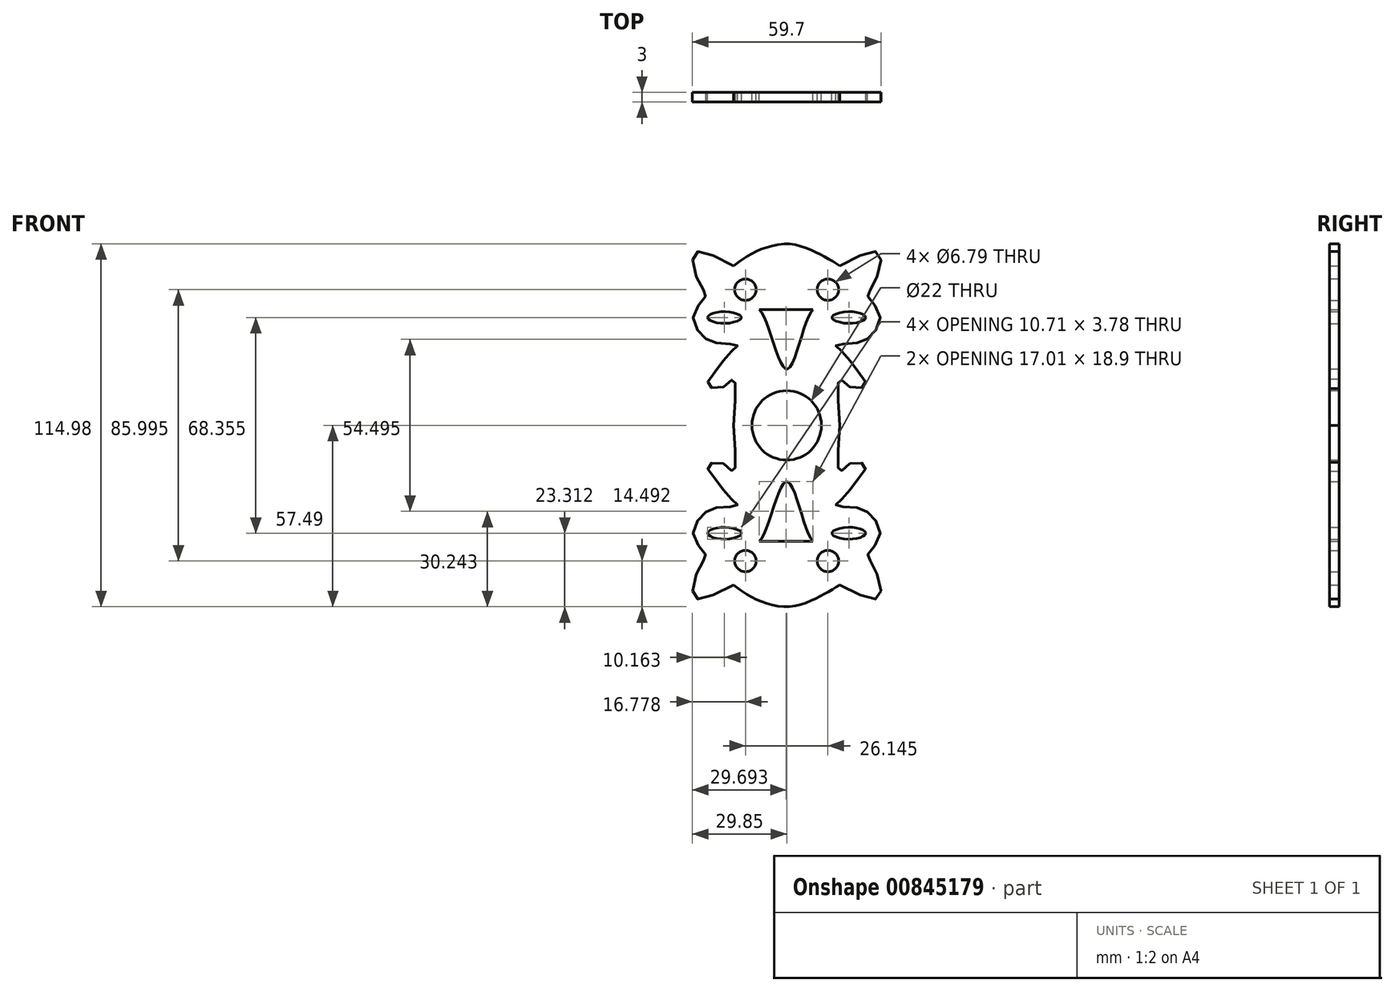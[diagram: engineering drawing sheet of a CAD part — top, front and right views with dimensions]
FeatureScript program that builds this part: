
annotation { "Feature Type Name" : "Feature", "Feature Type Description" : "" }
export const myFeature = defineFeature(function(context is Context, id is Id, definition is map)
    precondition{}
    {
        {
            var Q0;
            Q0=qCreatedBy(makeId("Front.planeOp"),FACE);
            var sketch = newSketch(context, id + "F0", { "sketchPlane" : qUnion([Q0])});
            skFitSpline(sketch, "E0", {"points": [v(-16.85, 50.56) * mm, v(-29.45, 54.34) * mm, v(-26.93, 43.63) * mm, v(-25.67, 41.1) * mm, v(-29.45, 35.44) * mm, v(-26.93, 28.5) * mm, v(-21.26, 25.99) * mm, v(-15.6, 25.36) * mm, v(-17.48, 23.47) * mm, v(-22.52, 17.17) * mm, v(-25.04, 12.76) * mm, v(-20, 12.13) * mm, v(-16.85, 14.65) * mm, v(-16.85, 0) * mm], "startDerivative": vector(-155.25, 81.9) * mm, "endDerivative": vector(-13.62, -190.37) * mm});
            skFitSpline(sketch, "E1.MirrorCS", {"points": [v(16.85, 50.56) * mm, v(29.45, 54.34) * mm, v(26.93, 43.63) * mm, v(25.67, 41.1) * mm, v(29.45, 35.44) * mm, v(26.93, 28.5) * mm, v(21.26, 25.99) * mm, v(15.6, 25.36) * mm, v(17.48, 23.47) * mm, v(22.52, 17.17) * mm, v(25.04, 12.76) * mm, v(20, 12.13) * mm, v(16.85, 14.65) * mm, v(16.85, 0) * mm], "startDerivative": vector(155.25, 81.9) * mm, "endDerivative": vector(13.62, -190.37) * mm});
            skFitSpline(sketch, "E2", {"points": [v(-16.85, 50.56) * mm, v(-11.18, 54.34) * mm, v(0, 57.49) * mm, v(10.24, 54.34) * mm, v(16.85, 50.56) * mm], "startDerivative": vector(23.07, 17.56) * mm, "endDerivative": vector(27.08, -16.35) * mm});
            skFitSpline(sketch, "E3.MirrorCS", {"points": [v(-16.85, -50.56) * mm, v(-11.18, -54.34) * mm, v(0, -57.49) * mm, v(10.24, -54.34) * mm, v(16.85, -50.56) * mm], "startDerivative": vector(23.07, -17.56) * mm, "endDerivative": vector(27.08, 16.35) * mm});
            skFitSpline(sketch, "E4.MirrorCS", {"points": [v(-16.85, -50.56) * mm, v(-29.45, -54.34) * mm, v(-26.93, -43.63) * mm, v(-25.67, -41.1) * mm, v(-29.45, -35.44) * mm, v(-26.93, -28.5) * mm, v(-21.26, -25.99) * mm, v(-15.6, -25.36) * mm, v(-17.48, -23.47) * mm, v(-22.52, -17.17) * mm, v(-25.04, -12.76) * mm, v(-20, -12.13) * mm, v(-16.85, -14.65) * mm, v(-16.85, 0) * mm], "startDerivative": vector(-155.25, -81.9) * mm, "endDerivative": vector(-13.62, 190.37) * mm});
            skFitSpline(sketch, "E5.MirrorCS", {"points": [v(16.85, -50.56) * mm, v(29.45, -54.34) * mm, v(26.93, -43.63) * mm, v(25.67, -41.1) * mm, v(29.45, -35.44) * mm, v(26.93, -28.5) * mm, v(21.26, -25.99) * mm, v(15.6, -25.36) * mm, v(17.48, -23.47) * mm, v(22.52, -17.17) * mm, v(25.04, -12.76) * mm, v(20, -12.13) * mm, v(16.85, -14.65) * mm, v(16.85, 0) * mm], "startDerivative": vector(155.25, -81.9) * mm, "endDerivative": vector(13.62, 190.37) * mm});
            skCircle(sketch, "E6", {"center": v(0, 0) * mm, "radius": 11 * mm});
            skCircle(sketch, "E7", {"center": v(-13.07, 43) * mm, "radius": 3.4 * mm});
            skCircle(sketch, "E8.MirrorC", {"center": v(13.07, 43) * mm, "radius": 3.4 * mm});
            skCircle(sketch, "E9.MirrorC", {"center": v(-13.07, -43) * mm, "radius": 3.4 * mm});
            skCircle(sketch, "E10.MirrorC", {"center": v(13.07, -43) * mm, "radius": 3.4 * mm});
            skLineSegment(sketch, "E11", {"start": v(-8.66, 36.7) * mm, "end": v(8.35, 36.7) * mm});
            skFitSpline(sketch, "E12", {"points": [v(-8.66, 36.7) * mm, v(0, 17.8) * mm, v(8.35, 36.7) * mm], "startDerivative": vector(17.3, -13.2) * mm, "endDerivative": vector(16.72, 13.26) * mm});
            skFitSpline(sketch, "E13.MirrorCS", {"points": [v(-8.66, -36.7) * mm, v(0, -17.8) * mm, v(8.35, -36.7) * mm], "startDerivative": vector(17.3, 13.2) * mm, "endDerivative": vector(16.72, -13.26) * mm});
            skLineSegment(sketch, "E14.MirrorCS", {"start": v(-8.66, -36.7) * mm, "end": v(8.35, -36.7) * mm});
            skFitSpline(sketch, "E15", {"points": [v(-25.04, 34.18) * mm, v(-20, 36.07) * mm, v(-14.33, 34.18) * mm, v(-20, 32.29) * mm, v(-25.04, 34.18) * mm]});
            skFitSpline(sketch, "E16.MirrorC", {"points": [v(25.04, 34.18) * mm, v(20, 36.07) * mm, v(14.33, 34.18) * mm, v(20, 32.29) * mm, v(25.04, 34.18) * mm]});
            skFitSpline(sketch, "E17.MirrorC", {"points": [v(-25.04, -34.18) * mm, v(-20, -36.07) * mm, v(-14.33, -34.18) * mm, v(-20, -32.29) * mm, v(-25.04, -34.18) * mm]});
            skFitSpline(sketch, "E18.MirrorC", {"points": [v(25.04, -34.18) * mm, v(20, -36.07) * mm, v(14.33, -34.18) * mm, v(20, -32.29) * mm, v(25.04, -34.18) * mm]});
            skSolve(sketch);
        }
        {
            var Q0;
            Q0 = qSketchRegion(id + "F0", true);
            extrude(context, id + "F1", {"entities" : qUnion([Q0]), "depth" : 3 * mm, "offsetDistance" : 25 * mm});
        }
    });
